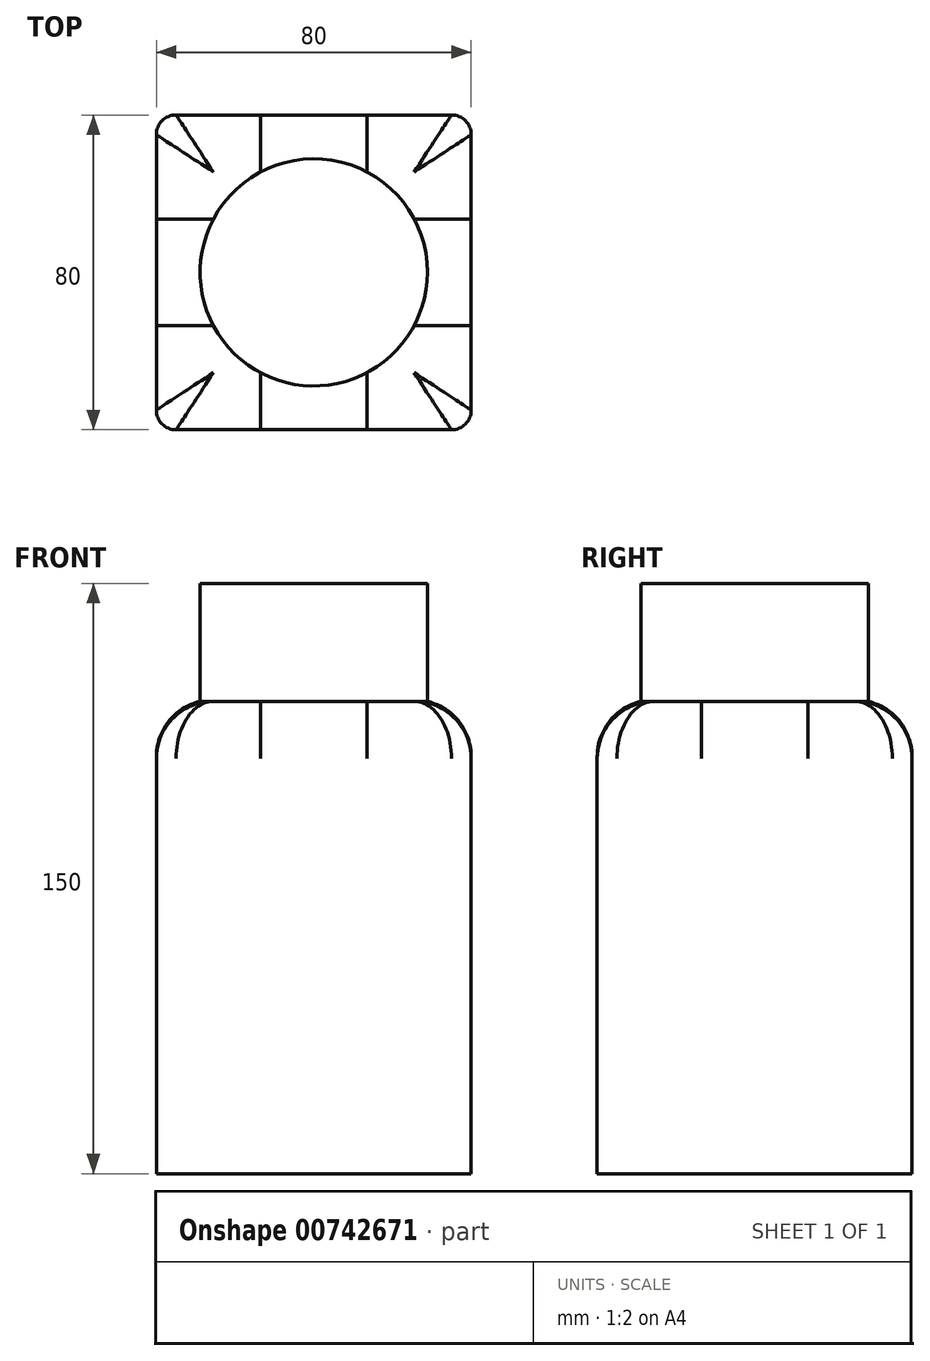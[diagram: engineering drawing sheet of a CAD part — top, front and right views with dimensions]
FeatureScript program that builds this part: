
annotation { "Feature Type Name" : "Feature", "Feature Type Description" : "" }
export const myFeature = defineFeature(function(context is Context, id is Id, definition is map)
    precondition{}
    {
        {
            var Q0;
            Q0=qCreatedBy(makeId("Top.planeOp"),FACE);
            var sketch = newSketch(context, id + "F0", { "sketchPlane" : qUnion([Q0])});
            skLineSegment(sketch, "E0", {"start": v(0, 40) * mm, "end": v(40, 40) * mm, "construction": true});
            skLineSegment(sketch, "E1", {"start": v(40, 40) * mm, "end": v(40, -40) * mm, "construction": true});
            skLineSegment(sketch, "E2", {"start": v(0, 40) * mm, "end": v(40, 40) * mm});
            skLineSegment(sketch, "E3", {"start": v(40, 40) * mm, "end": v(40, -40) * mm});
            skLineSegment(sketch, "E4", {"start": v(40, -40) * mm, "end": v(0, -40) * mm});
            skLineSegment(sketch, "E5.MirrorCS", {"start": v(0, 40) * mm, "end": v(-40, 40) * mm});
            skLineSegment(sketch, "E6.MirrorCS", {"start": v(-40, 40) * mm, "end": v(-40, -40) * mm});
            skLineSegment(sketch, "E7.MirrorCS", {"start": v(-40, -40) * mm, "end": v(0, -40) * mm});
            skSolve(sketch);
        }
        {
            var Q0;
            Q0=makeQuery(id+"F0.imprint","IMPRINT",FACE,{"disambiguationData":[TD([[makeQuery(id+"F0.imprint","IMPRINT",EDGE,{"derivedFrom":sQuery(id+"F0.wireOp",EDGE,"E2")}),-1.0]])]});
            extrude(context, id + "F1", {"entities" : qUnion([Q0]), "depth" : 120 * mm, "offsetDistance" : 25 * mm});
        }
        {
            var Q0;
            Q0=makeQuery(id+"F1.opExtrude","CAP_FACE",FACE,{"disambiguationData":[OSD([sQuery(id+"F0.wireOp",EDGE,"E2"),sQuery(id+"F0.wireOp",EDGE,"E3"),sQuery(id+"F0.wireOp",EDGE,"E4"),sQuery(id+"F0.wireOp",EDGE,"E5.MirrorCS"),sQuery(id+"F0.wireOp",EDGE,"E6.MirrorCS"),sQuery(id+"F0.wireOp",EDGE,"E7.MirrorCS")])],"isStart":false});
            var sketch = newSketch(context, id + "F2", { "sketchPlane" : qUnion([Q0])});
            skCircle(sketch, "E8", {"center": v(0, 0) * mm, "radius": 28.87 * mm});
            skSolve(sketch);
        }
        {
            var Q0;
            Q0 = qSketchRegion(id + "F2", true);
            extrude(context, id + "F3", {"entities" : qUnion([Q0]), "operationType" : NewBodyOperationType.ADD, "depth" : 30 * mm, "offsetDistance" : 25 * mm});
        }
        {
            var Q0;
            Q0=makeQuery(id+"F1.opExtrude","CAP_EDGE",EDGE,{"disambiguationData":[OSD([sQuery(id+"F0.wireOp",EDGE,"E4"),sQuery(id+"F0.wireOp",EDGE,"E7.MirrorCS")])],"isStart":false});
            var Q1;
            Q1=makeQuery(id+"F1.opExtrude","CAP_EDGE",EDGE,{"disambiguationData":[OSD([sQuery(id+"F0.wireOp",EDGE,"E6.MirrorCS")])],"isStart":false});
            var Q2;
            Q2=makeQuery(id+"F1.opExtrude","CAP_EDGE",EDGE,{"disambiguationData":[OSD([sQuery(id+"F0.wireOp",EDGE,"E3")])],"isStart":false});
            var Q3;
            Q3=makeQuery(id+"F1.opExtrude","CAP_EDGE",EDGE,{"disambiguationData":[OSD([sQuery(id+"F0.wireOp",EDGE,"E2"),sQuery(id+"F0.wireOp",EDGE,"E5.MirrorCS")])],"isStart":false});
            fillet(context, id + "F4", {"entities" : qUnion([Q0, Q1, Q2, Q3]), "radius" : 14.5 * mm, "tangentPropagation" : true, "allowEdgeOverflow" : false});
        }
        {
            var Q0;
            Q0=makeQuery(id+"F4.opFillet","BLEND_EDGE",EDGE,{"blendedFrom":[makeQuery(id+"F1.opExtrude","CAP_EDGE",EDGE,{"disambiguationData":[OSD([sQuery(id+"F0.wireOp",EDGE,"E4"),sQuery(id+"F0.wireOp",EDGE,"E7.MirrorCS")])],"isStart":false}),makeQuery(id+"F1.opExtrude","CAP_EDGE",EDGE,{"disambiguationData":[OSD([sQuery(id+"F0.wireOp",EDGE,"E6.MirrorCS")])],"isStart":false})],"blendedInto":[]});
            var Q1;
            Q1=makeQuery(id+"F4.opFillet","BLEND_EDGE",EDGE,{"blendedFrom":[makeQuery(id+"F1.opExtrude","CAP_EDGE",EDGE,{"disambiguationData":[OSD([sQuery(id+"F0.wireOp",EDGE,"E3")])],"isStart":false}),makeQuery(id+"F1.opExtrude","CAP_EDGE",EDGE,{"disambiguationData":[OSD([sQuery(id+"F0.wireOp",EDGE,"E4"),sQuery(id+"F0.wireOp",EDGE,"E7.MirrorCS")])],"isStart":false})],"blendedInto":[]});
            var Q2;
            Q2=makeQuery(id+"F4.opFillet","BLEND_EDGE",EDGE,{"blendedFrom":[makeQuery(id+"F1.opExtrude","CAP_EDGE",EDGE,{"disambiguationData":[OSD([sQuery(id+"F0.wireOp",EDGE,"E2"),sQuery(id+"F0.wireOp",EDGE,"E5.MirrorCS")])],"isStart":false}),makeQuery(id+"F1.opExtrude","CAP_EDGE",EDGE,{"disambiguationData":[OSD([sQuery(id+"F0.wireOp",EDGE,"E3")])],"isStart":false})],"blendedInto":[]});
            var Q3;
            Q3=makeQuery(id+"F4.opFillet","BLEND_EDGE",EDGE,{"blendedFrom":[makeQuery(id+"F1.opExtrude","CAP_EDGE",EDGE,{"disambiguationData":[OSD([sQuery(id+"F0.wireOp",EDGE,"E2"),sQuery(id+"F0.wireOp",EDGE,"E5.MirrorCS")])],"isStart":false}),makeQuery(id+"F1.opExtrude","CAP_EDGE",EDGE,{"disambiguationData":[OSD([sQuery(id+"F0.wireOp",EDGE,"E6.MirrorCS")])],"isStart":false})],"blendedInto":[]});
            fillet(context, id + "F5", {"entities" : qUnion([Q0, Q1, Q2, Q3]), "radius" : 5 * mm, "tangentPropagation" : true, "allowEdgeOverflow" : false});
        }
    });
